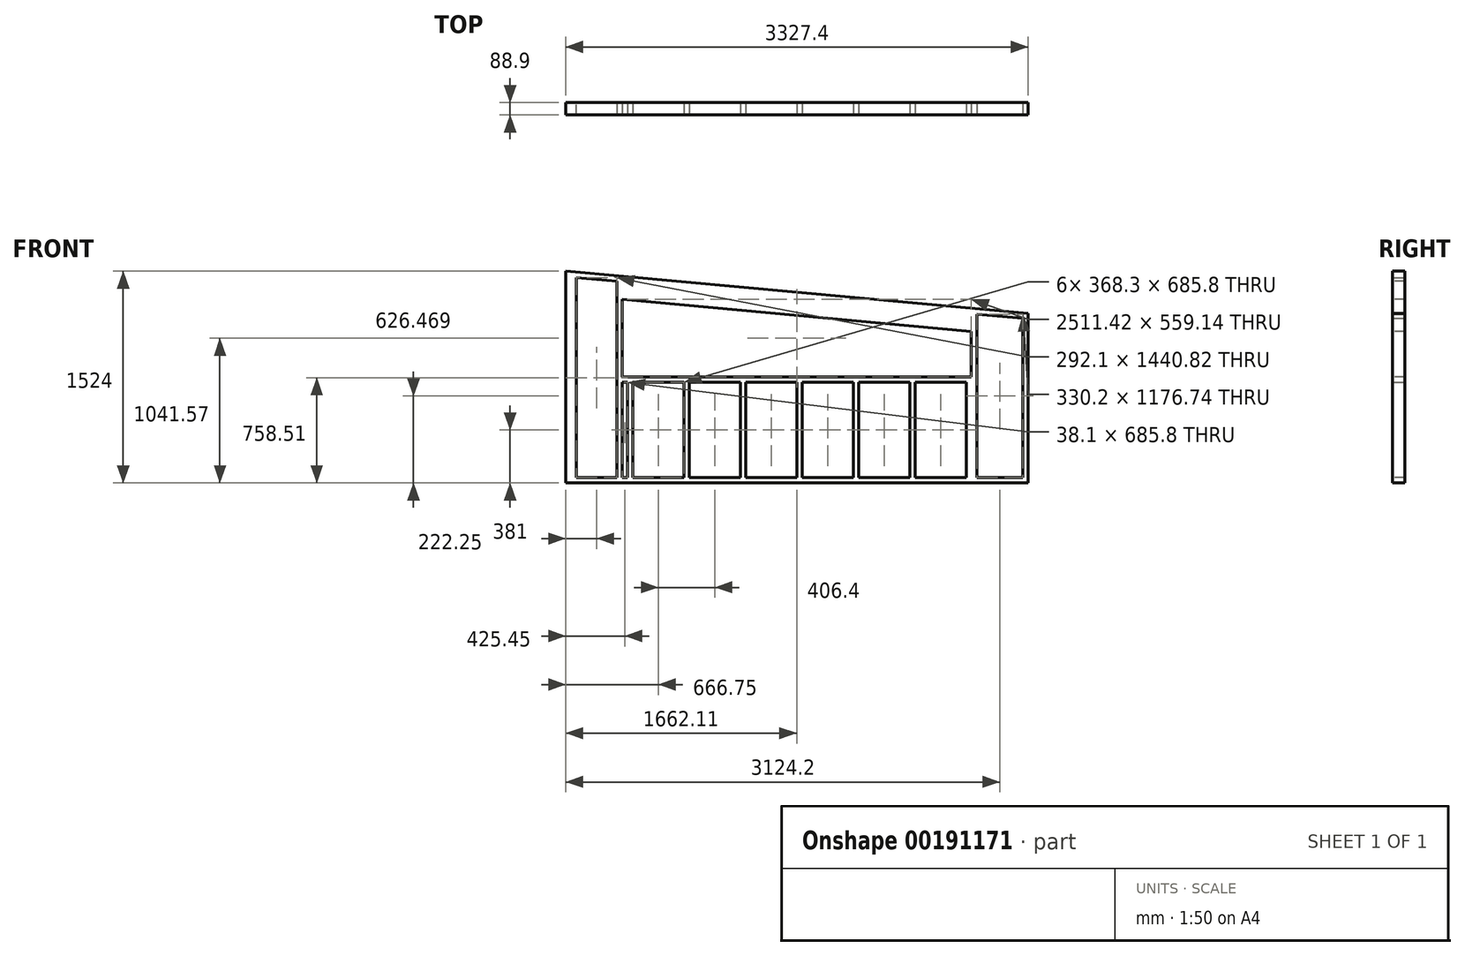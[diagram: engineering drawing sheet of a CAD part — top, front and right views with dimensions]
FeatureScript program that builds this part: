
annotation { "Feature Type Name" : "Feature", "Feature Type Description" : "" }
export const myFeature = defineFeature(function(context is Context, id is Id, definition is map)
    precondition{}
    {
        {
            var Q0;
            Q0=qCreatedBy(makeId("Top.planeOp"),FACE);
            var sketch = newSketch(context, id + "F0", { "sketchPlane" : qUnion([Q0])});
            skLineSegment(sketch, "E0.bottom", {"start": v(1663.7, -44.45) * mm, "end": v(-1663.7, -44.45) * mm});
            skLineSegment(sketch, "E0.top", {"start": v(1663.7, 44.45) * mm, "end": v(-1663.7, 44.45) * mm});
            skLineSegment(sketch, "E0.left", {"start": v(1663.7, -44.45) * mm, "end": v(1663.7, 44.45) * mm});
            skLineSegment(sketch, "E0.right", {"start": v(-1663.7, -44.45) * mm, "end": v(-1663.7, 44.45) * mm});
            skPoint(sketch, "E0.middle", {"position": v(0, 0) * mm});
            skSolve(sketch);
        }
        {
            var Q0;
            Q0 = qSketchRegion(id + "F0", true);
            extrude(context, id + "F1", {"entities" : qUnion([Q0]), "depth" : 38.1 * mm});
        }
        {
            var Q0;
            Q0=makeQuery(id+"F1.opExtrude","CAP_FACE",FACE,{"disambiguationData":[OSD([sQuery(id+"F0.wireOp",EDGE,"E0.bottom"),sQuery(id+"F0.wireOp",EDGE,"E0.top"),sQuery(id+"F0.wireOp",EDGE,"E0.left"),sQuery(id+"F0.wireOp",EDGE,"E0.right")])],"isStart":false});
            var sketch = newSketch(context, id + "F2", { "sketchPlane" : qUnion([Q0])});
            skLineSegment(sketch, "E1.bottom", {"start": v(1663.7, 44.45) * mm, "end": v(1625.6, 44.45) * mm});
            skLineSegment(sketch, "E1.top", {"start": v(1663.7, -44.45) * mm, "end": v(1625.6, -44.45) * mm});
            skLineSegment(sketch, "E1.left", {"start": v(1663.7, 44.45) * mm, "end": v(1663.7, -44.45) * mm});
            skLineSegment(sketch, "E1.right", {"start": v(1625.6, 44.45) * mm, "end": v(1625.6, -44.45) * mm});
            skLineSegment(sketch, "E2.bottom", {"start": v(1257.3, 44.45) * mm, "end": v(1219.2, 44.45) * mm});
            skLineSegment(sketch, "E2.top", {"start": v(1257.3, -44.45) * mm, "end": v(1219.2, -44.45) * mm});
            skLineSegment(sketch, "E2.left", {"start": v(1257.3, 44.45) * mm, "end": v(1257.3, -44.45) * mm});
            skLineSegment(sketch, "E2.right", {"start": v(1219.2, 44.45) * mm, "end": v(1219.2, -44.45) * mm});
            skLineSegment(sketch, "E3.bottom", {"start": v(850.9, 44.45) * mm, "end": v(812.8, 44.45) * mm});
            skLineSegment(sketch, "E3.top", {"start": v(850.9, -44.45) * mm, "end": v(812.8, -44.45) * mm});
            skLineSegment(sketch, "E3.left", {"start": v(850.9, 44.45) * mm, "end": v(850.9, -44.45) * mm});
            skLineSegment(sketch, "E3.right", {"start": v(812.8, 44.45) * mm, "end": v(812.8, -44.45) * mm});
            skLineSegment(sketch, "E4.bottom", {"start": v(444.5, 44.45) * mm, "end": v(406.4, 44.45) * mm});
            skLineSegment(sketch, "E4.top", {"start": v(444.5, -44.45) * mm, "end": v(406.4, -44.45) * mm});
            skLineSegment(sketch, "E4.left", {"start": v(444.5, 44.45) * mm, "end": v(444.5, -44.45) * mm});
            skLineSegment(sketch, "E4.right", {"start": v(406.4, 44.45) * mm, "end": v(406.4, -44.45) * mm});
            skLineSegment(sketch, "E5.bottom", {"start": v(38.1, 44.45) * mm, "end": v(0, 44.45) * mm});
            skLineSegment(sketch, "E5.top", {"start": v(38.1, -44.45) * mm, "end": v(0, -44.45) * mm});
            skLineSegment(sketch, "E5.left", {"start": v(38.1, 44.45) * mm, "end": v(38.1, -44.45) * mm});
            skLineSegment(sketch, "E5.right", {"start": v(0, 44.45) * mm, "end": v(0, -44.45) * mm});
            skLineSegment(sketch, "E6.bottom", {"start": v(-368.3, 44.45) * mm, "end": v(-406.4, 44.45) * mm});
            skLineSegment(sketch, "E6.top", {"start": v(-368.3, -44.45) * mm, "end": v(-406.4, -44.45) * mm});
            skLineSegment(sketch, "E6.left", {"start": v(-368.3, 44.45) * mm, "end": v(-368.3, -44.45) * mm});
            skLineSegment(sketch, "E6.right", {"start": v(-406.4, 44.45) * mm, "end": v(-406.4, -44.45) * mm});
            skLineSegment(sketch, "E7.bottom", {"start": v(-774.7, 44.45) * mm, "end": v(-812.8, 44.45) * mm});
            skLineSegment(sketch, "E7.top", {"start": v(-774.7, -44.45) * mm, "end": v(-812.8, -44.45) * mm});
            skLineSegment(sketch, "E7.left", {"start": v(-774.7, 44.45) * mm, "end": v(-774.7, -44.45) * mm});
            skLineSegment(sketch, "E7.right", {"start": v(-812.8, 44.45) * mm, "end": v(-812.8, -44.45) * mm});
            skLineSegment(sketch, "E8.bottom", {"start": v(-1181.1, 44.45) * mm, "end": v(-1219.2, 44.45) * mm});
            skLineSegment(sketch, "E8.top", {"start": v(-1181.1, -44.45) * mm, "end": v(-1219.2, -44.45) * mm});
            skLineSegment(sketch, "E8.left", {"start": v(-1181.1, 44.45) * mm, "end": v(-1181.1, -44.45) * mm});
            skLineSegment(sketch, "E8.right", {"start": v(-1219.2, 44.45) * mm, "end": v(-1219.2, -44.45) * mm});
            skLineSegment(sketch, "E9.bottom", {"start": v(-1663.7, 44.45) * mm, "end": v(-1625.6, 44.45) * mm});
            skLineSegment(sketch, "E9.top", {"start": v(-1663.7, -44.45) * mm, "end": v(-1625.6, -44.45) * mm});
            skLineSegment(sketch, "E9.left", {"start": v(-1663.7, 44.45) * mm, "end": v(-1663.7, -44.45) * mm});
            skLineSegment(sketch, "E9.right", {"start": v(-1625.6, 44.45) * mm, "end": v(-1625.6, -44.45) * mm});
            skLineSegment(sketch, "E10.bottom", {"start": v(-1625.6, 44.45) * mm, "end": v(-1587.5, 44.45) * mm});
            skLineSegment(sketch, "E10.top", {"start": v(-1625.6, -44.45) * mm, "end": v(-1587.5, -44.45) * mm});
            skLineSegment(sketch, "E10.right", {"start": v(-1587.5, 44.45) * mm, "end": v(-1587.5, -44.45) * mm});
            skSolve(sketch);
        }
        {
            var Q0;
            Q0 = qSketchRegion(id + "F2", true);
            extrude(context, id + "F3", {"entities" : qUnion([Q0]), "operationType" : NewBodyOperationType.ADD, "depth" : 1524 * mm});
        }
        {
            var Q0;
            Q0=makeQuery(id+"F3.boolean.opBoolean","MERGE",FACE,{"derivedFrom":[makeQuery(id+"F1.opExtrude","SWEPT_FACE",FACE,{"disambiguationData":[OSD([sQuery(id+"F0.wireOp",EDGE,"E0.bottom")])]}),makeQuery(id+"F3.opExtrude","SWEPT_FACE",FACE,{"disambiguationData":[OSD([sQuery(id+"F2.wireOp",EDGE,"E1.top")])]}),makeQuery(id+"F3.opExtrude","SWEPT_FACE",FACE,{"disambiguationData":[OSD([sQuery(id+"F2.wireOp",EDGE,"E2.top")])]}),makeQuery(id+"F3.opExtrude","SWEPT_FACE",FACE,{"disambiguationData":[OSD([sQuery(id+"F2.wireOp",EDGE,"E3.top")])]}),makeQuery(id+"F3.opExtrude","SWEPT_FACE",FACE,{"disambiguationData":[OSD([sQuery(id+"F2.wireOp",EDGE,"E4.top")])]}),makeQuery(id+"F3.opExtrude","SWEPT_FACE",FACE,{"disambiguationData":[OSD([sQuery(id+"F2.wireOp",EDGE,"E5.top")])]}),makeQuery(id+"F3.opExtrude","SWEPT_FACE",FACE,{"disambiguationData":[OSD([sQuery(id+"F2.wireOp",EDGE,"E6.top")])]}),makeQuery(id+"F3.opExtrude","SWEPT_FACE",FACE,{"disambiguationData":[OSD([sQuery(id+"F2.wireOp",EDGE,"E7.top")])]}),makeQuery(id+"F3.opExtrude","SWEPT_FACE",FACE,{"disambiguationData":[OSD([sQuery(id+"F2.wireOp",EDGE,"E8.top")])]}),makeQuery(id+"F3.opExtrude","SWEPT_FACE",FACE,{"disambiguationData":[OSD([sQuery(id+"F2.wireOp",EDGE,"E9.top"),sQuery(id+"F2.wireOp",EDGE,"E10.top")])]})]});
            var sketch = newSketch(context, id + "F4", { "sketchPlane" : qUnion([Q0])});
            skLineSegment(sketch, "E11", {"start": v(-1663.7, 1485.9) * mm, "end": v(1663.7, 1181.1) * mm});
            skLineSegment(sketch, "E12", {"start": v(1663.7, 1181.1) * mm, "end": v(1733.68, 1945) * mm});
            skLineSegment(sketch, "E13", {"start": v(1733.68, 1945) * mm, "end": v(-1823.17, 1997.78) * mm});
            skLineSegment(sketch, "E14", {"start": v(-1823.17, 1997.78) * mm, "end": v(-1663.7, 1485.9) * mm});
            skSolve(sketch);
        }
        {
            var Q0;
            Q0 = qSketchRegion(id + "F4", true);
            extrude(context, id + "F5", {"entities" : qUnion([Q0]), "operationType" : NewBodyOperationType.REMOVE, "oppositeDirection" : true, "depth" : 431.8 * mm});
        }
        {
            var Q0;
            Q0=makeQuery(id+"F3.boolean.opBoolean","MERGE",FACE,{"derivedFrom":[makeQuery(id+"F1.opExtrude","SWEPT_FACE",FACE,{"disambiguationData":[OSD([sQuery(id+"F0.wireOp",EDGE,"E0.bottom")])]}),makeQuery(id+"F3.opExtrude","SWEPT_FACE",FACE,{"disambiguationData":[OSD([sQuery(id+"F2.wireOp",EDGE,"E1.top")])]}),makeQuery(id+"F3.opExtrude","SWEPT_FACE",FACE,{"disambiguationData":[OSD([sQuery(id+"F2.wireOp",EDGE,"E2.top")])]}),makeQuery(id+"F3.opExtrude","SWEPT_FACE",FACE,{"disambiguationData":[OSD([sQuery(id+"F2.wireOp",EDGE,"E3.top")])]}),makeQuery(id+"F3.opExtrude","SWEPT_FACE",FACE,{"disambiguationData":[OSD([sQuery(id+"F2.wireOp",EDGE,"E4.top")])]}),makeQuery(id+"F3.opExtrude","SWEPT_FACE",FACE,{"disambiguationData":[OSD([sQuery(id+"F2.wireOp",EDGE,"E5.top")])]}),makeQuery(id+"F3.opExtrude","SWEPT_FACE",FACE,{"disambiguationData":[OSD([sQuery(id+"F2.wireOp",EDGE,"E6.top")])]}),makeQuery(id+"F3.opExtrude","SWEPT_FACE",FACE,{"disambiguationData":[OSD([sQuery(id+"F2.wireOp",EDGE,"E7.top")])]}),makeQuery(id+"F3.opExtrude","SWEPT_FACE",FACE,{"disambiguationData":[OSD([sQuery(id+"F2.wireOp",EDGE,"E8.top")])]}),makeQuery(id+"F3.opExtrude","SWEPT_FACE",FACE,{"disambiguationData":[OSD([sQuery(id+"F2.wireOp",EDGE,"E9.top"),sQuery(id+"F2.wireOp",EDGE,"E10.top")])]})]});
            var sketch = newSketch(context, id + "F6", { "sketchPlane" : qUnion([Q0])});
            skLineSegment(sketch, "E15", {"start": v(-1663.7, 1485.9) * mm, "end": v(1663.7, 1181.1) * mm});
            skLineSegment(sketch, "E16", {"start": v(1663.7, 1181.1) * mm, "end": v(1663.7, 1219.2) * mm});
            skLineSegment(sketch, "E17", {"start": v(1663.7, 1219.2) * mm, "end": v(-1663.7, 1524) * mm});
            skLineSegment(sketch, "E18", {"start": v(-1663.7, 1524) * mm, "end": v(-1663.7, 1485.9) * mm});
            skSolve(sketch);
        }
        {
            var Q0;
            Q0 = qSketchRegion(id + "F6", true);
            extrude(context, id + "F7", {"entities" : qUnion([Q0]), "operationType" : NewBodyOperationType.ADD, "oppositeDirection" : true, "depth" : 88.9 * mm});
        }
        {
            var Q0;
            Q0=makeQuery(id+"F7.boolean.opBoolean","MERGE",FACE,{"derivedFrom":[makeQuery(id+"F3.boolean.opBoolean","MERGE",FACE,{"derivedFrom":[makeQuery(id+"F1.opExtrude","SWEPT_FACE",FACE,{"disambiguationData":[OSD([sQuery(id+"F0.wireOp",EDGE,"E0.bottom")])]}),makeQuery(id+"F3.opExtrude","SWEPT_FACE",FACE,{"disambiguationData":[OSD([sQuery(id+"F2.wireOp",EDGE,"E1.top")])]}),makeQuery(id+"F3.opExtrude","SWEPT_FACE",FACE,{"disambiguationData":[OSD([sQuery(id+"F2.wireOp",EDGE,"E2.top")])]}),makeQuery(id+"F3.opExtrude","SWEPT_FACE",FACE,{"disambiguationData":[OSD([sQuery(id+"F2.wireOp",EDGE,"E3.top")])]}),makeQuery(id+"F3.opExtrude","SWEPT_FACE",FACE,{"disambiguationData":[OSD([sQuery(id+"F2.wireOp",EDGE,"E4.top")])]}),makeQuery(id+"F3.opExtrude","SWEPT_FACE",FACE,{"disambiguationData":[OSD([sQuery(id+"F2.wireOp",EDGE,"E5.top")])]}),makeQuery(id+"F3.opExtrude","SWEPT_FACE",FACE,{"disambiguationData":[OSD([sQuery(id+"F2.wireOp",EDGE,"E6.top")])]}),makeQuery(id+"F3.opExtrude","SWEPT_FACE",FACE,{"disambiguationData":[OSD([sQuery(id+"F2.wireOp",EDGE,"E7.top")])]}),makeQuery(id+"F3.opExtrude","SWEPT_FACE",FACE,{"disambiguationData":[OSD([sQuery(id+"F2.wireOp",EDGE,"E8.top")])]}),makeQuery(id+"F3.opExtrude","SWEPT_FACE",FACE,{"disambiguationData":[OSD([sQuery(id+"F2.wireOp",EDGE,"E9.top"),sQuery(id+"F2.wireOp",EDGE,"E10.top")])]})]}),makeQuery(id+"F7.opExtrude","CAP_FACE",FACE,{"disambiguationData":[OSD([sQuery(id+"F6.wireOp",EDGE,"E15"),sQuery(id+"F6.wireOp",EDGE,"E16"),sQuery(id+"F6.wireOp",EDGE,"E17"),sQuery(id+"F6.wireOp",EDGE,"E18")])],"isStart":true})]});
            var sketch = newSketch(context, id + "F8", { "sketchPlane" : qUnion([Q0])});
            skLineSegment(sketch, "E19", {"start": v(-1257.3, 762) * mm, "end": v(1257.3, 762) * mm});
            skLineSegment(sketch, "E20", {"start": v(1257.3, 762) * mm, "end": v(1257.3, 1090.8) * mm});
            skLineSegment(sketch, "E21", {"start": v(1257.3, 1090.8) * mm, "end": v(-1257.3, 1321.14) * mm});
            skLineSegment(sketch, "E22", {"start": v(-1257.3, 1321.14) * mm, "end": v(-1257.3, 762) * mm});
            skLineSegment(sketch, "E23.bottom", {"start": v(-1257.3, 38.1) * mm, "end": v(-1295.4, 38.1) * mm});
            skLineSegment(sketch, "E23.top", {"start": v(-1257.3, 1452.16) * mm, "end": v(-1295.4, 1452.16) * mm});
            skLineSegment(sketch, "E23.left", {"start": v(-1257.3, 38.1) * mm, "end": v(-1257.3, 1452.16) * mm});
            skLineSegment(sketch, "E23.right", {"start": v(-1295.4, 38.1) * mm, "end": v(-1295.4, 1452.16) * mm});
            skLineSegment(sketch, "E24.bottom", {"start": v(1257.3, 1218.33) * mm, "end": v(1295.4, 1218.33) * mm});
            skLineSegment(sketch, "E24.top", {"start": v(1257.3, 38.1) * mm, "end": v(1295.4, 38.1) * mm});
            skLineSegment(sketch, "E24.left", {"start": v(1257.3, 1218.33) * mm, "end": v(1257.3, 38.1) * mm});
            skLineSegment(sketch, "E24.right", {"start": v(1295.4, 1218.33) * mm, "end": v(1295.4, 38.1) * mm});
            skLineSegment(sketch, "E25.top", {"start": v(-1257.3, 723.9) * mm, "end": v(1257.3, 723.9) * mm});
            skLineSegment(sketch, "E25.left", {"start": v(-1257.3, 762) * mm, "end": v(-1257.3, 723.9) * mm});
            skLineSegment(sketch, "E25.right", {"start": v(1257.3, 762) * mm, "end": v(1257.3, 723.9) * mm});
            skLineSegment(sketch, "E26", {"start": v(1257.3, 1218.33) * mm, "end": v(-1257.3, 1452.16) * mm});
            skLineSegment(sketch, "E27", {"start": v(-1257.3, 1321.14) * mm, "end": v(1257.3, 1090.8) * mm});
            skSolve(sketch);
        }
        {
            var Q0;
            Q0 = qSketchRegion(id + "F8", true);
            extrude(context, id + "F9", {"entities" : qUnion([Q0]), "operationType" : NewBodyOperationType.ADD, "oppositeDirection" : true, "depth" : 88.9 * mm});
        }
        {
            var Q0;
            Q0=makeQuery(id+"F9.boolean.opBoolean","MERGE",FACE,{"derivedFrom":[makeQuery(id+"F7.boolean.opBoolean","MERGE",FACE,{"derivedFrom":[makeQuery(id+"F3.boolean.opBoolean","MERGE",FACE,{"derivedFrom":[makeQuery(id+"F1.opExtrude","SWEPT_FACE",FACE,{"disambiguationData":[OSD([sQuery(id+"F0.wireOp",EDGE,"E0.bottom")])]}),makeQuery(id+"F3.opExtrude","SWEPT_FACE",FACE,{"disambiguationData":[OSD([sQuery(id+"F2.wireOp",EDGE,"E1.top")])]}),makeQuery(id+"F3.opExtrude","SWEPT_FACE",FACE,{"disambiguationData":[OSD([sQuery(id+"F2.wireOp",EDGE,"E2.top")])]}),makeQuery(id+"F3.opExtrude","SWEPT_FACE",FACE,{"disambiguationData":[OSD([sQuery(id+"F2.wireOp",EDGE,"E3.top")])]}),makeQuery(id+"F3.opExtrude","SWEPT_FACE",FACE,{"disambiguationData":[OSD([sQuery(id+"F2.wireOp",EDGE,"E4.top")])]}),makeQuery(id+"F3.opExtrude","SWEPT_FACE",FACE,{"disambiguationData":[OSD([sQuery(id+"F2.wireOp",EDGE,"E5.top")])]}),makeQuery(id+"F3.opExtrude","SWEPT_FACE",FACE,{"disambiguationData":[OSD([sQuery(id+"F2.wireOp",EDGE,"E6.top")])]}),makeQuery(id+"F3.opExtrude","SWEPT_FACE",FACE,{"disambiguationData":[OSD([sQuery(id+"F2.wireOp",EDGE,"E7.top")])]}),makeQuery(id+"F3.opExtrude","SWEPT_FACE",FACE,{"disambiguationData":[OSD([sQuery(id+"F2.wireOp",EDGE,"E8.top")])]}),makeQuery(id+"F3.opExtrude","SWEPT_FACE",FACE,{"disambiguationData":[OSD([sQuery(id+"F2.wireOp",EDGE,"E9.top"),sQuery(id+"F2.wireOp",EDGE,"E10.top")])]})]}),makeQuery(id+"F7.opExtrude","CAP_FACE",FACE,{"disambiguationData":[OSD([sQuery(id+"F6.wireOp",EDGE,"E15"),sQuery(id+"F6.wireOp",EDGE,"E16"),sQuery(id+"F6.wireOp",EDGE,"E17"),sQuery(id+"F6.wireOp",EDGE,"E18")])],"isStart":true})]}),makeQuery(id+"F9.opExtrude","CAP_FACE",FACE,{"disambiguationData":[OSD([sQuery(id+"F8.wireOp",EDGE,"E23.bottom"),sQuery(id+"F8.wireOp",EDGE,"E23.top"),sQuery(id+"F8.wireOp",EDGE,"E23.left"),sQuery(id+"F8.wireOp",EDGE,"E23.right"),sQuery(id+"F8.wireOp",EDGE,"E24.bottom"),sQuery(id+"F8.wireOp",EDGE,"E24.top"),sQuery(id+"F8.wireOp",EDGE,"E24.left"),sQuery(id+"F8.wireOp",EDGE,"E24.right"),sQuery(id+"F8.wireOp",EDGE,"E19"),sQuery(id+"F8.wireOp",EDGE,"E25.top"),sQuery(id+"F8.wireOp",EDGE,"E26"),sQuery(id+"F8.wireOp",EDGE,"E27")])],"isStart":true})]});
            var sketch = newSketch(context, id + "F10", { "sketchPlane" : qUnion([Q0])});
            skLineSegment(sketch, "E28", {"start": v(-1257.3, 762) * mm, "end": v(1254.12, 762) * mm});
            skLineSegment(sketch, "E29", {"start": v(1254.12, 762) * mm, "end": v(1254.12, 1094.29) * mm});
            skLineSegment(sketch, "E30", {"start": v(-1257.3, 762) * mm, "end": v(-1257.3, 1321.14) * mm});
            skLineSegment(sketch, "E31", {"start": v(-1257.3, 1321.14) * mm, "end": v(1254.12, 1091.09) * mm});
            skSolve(sketch);
        }
        {
            var Q0;
            Q0 = qSketchRegion(id + "F10", true);
            extrude(context, id + "F11", {"entities" : qUnion([Q0]), "operationType" : NewBodyOperationType.REMOVE, "oppositeDirection" : true, "depth" : 330.2 * mm});
        }
    });
